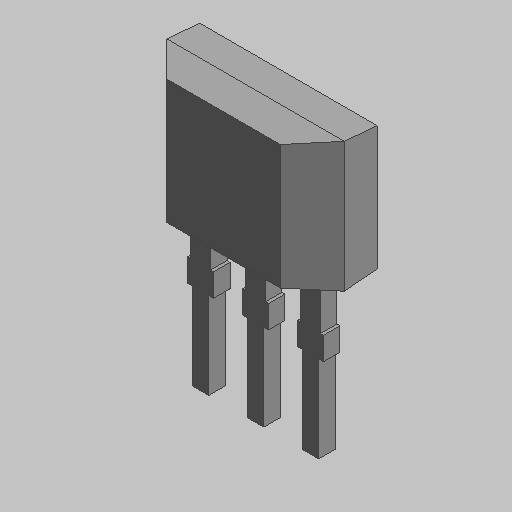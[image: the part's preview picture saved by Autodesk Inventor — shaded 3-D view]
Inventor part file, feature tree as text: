
AUTODESK INVENTOR PART (.ipt)
format: ipt  version: 2023.5 (Build 275446000, 446)  size: 79,360 bytes
history: native  units: mm (DEFAULTED — no unit token found)
features: extrude x1
ambient origin geometry x8: Origin, YZ Plane, XZ Plane, XY Plane, X Axis, Y Axis, Z Axis, Center Point
bodies: Solid1 (feature_tree)
feature tree (1):
  extrude  "Extrude2"  [1 undecoded]
note: 1 required parameter value undecoded (feature->parameter linkage not recoverable at this tier; creation-order binding heuristic only, values carry confidence <= 0.55)
